# Revit family: Hager-Volta-IP30-Flush_mounted-vuoto-CH-it
name_source: partatom
category: Electrical Equipment
units: mm (PartAtom-declared; Revit-internal decimal feet)

## family parameters
Cut with Voids When Loaded = No
Host = Face
Panel Configuration = Two Columns, Circuits Across
Part Type = Panelboard
Room Calculation Point = No
Round Connector Dimension = Use Diameter
Shared = No

## types (5) — shared parameters
EF000003 - Tipo di montaggio = EV000383 - incassato
EF000007 - colore = EV000270 - grigio
EF000049 - profondità = 94 mm  [stored 0.308399 ft]
EF000116 - numero RAL = 7035
EF000118 - con piastra di montaggio = No
EF000218 - profondità di incasso = 90 mm  [stored 0.295276 ft]
EF000846 - larghezza di montaggio = 335 mm  [stored 1.09908 ft]
EF001062 - esecuzione EMC = Yes
EF001088 - possibilità di applicazione = Yes
EF001131 - profondità interna = 92 mm
EF001134 - barra DIN = No
EF001596 - Attacco Lampada = EV000139 - plastica
EF002950 - Numero moduli DIN = 12
EF006244 - coperchio/porta trasparente = No
EF006306 - con serratura = No
EF009212 - esecuzione coperchio = EV000116 - chiuso
EF015776 - Morsettiera di terra = No
EF015777 - Morsettiera neutra = No
EF015941 - Segnale di passaggio porta = No
HG000002 - Con porta = No
HG000003 - Gamma = Volta
HG000005 - Spessore = 3 mm  [stored 0.00984252 ft]
HG000006 - Ad incasso = Yes
HG000009 - Porta doppia a battente = No
HG000010 - Porte asimmetriche = No
HG000011 - File vuote nella parte basse = No
HG000017 - Distanza tra i poli = 18 mm  [stored 0.0590551 ft]
Manufacturer = Hager
Type Comments = Volta
zero-valued in all types: Default Elevation, HG000001 - Numero di colonne, HG000007 - Numero di colonne vuote, HG000008 - Numero di file vuote

## per-type parameters (varying)
| type | EF000008 - Larghezza | EF000040 - Altezza | EF000266 - numero di file | EF000332 - Altezza della parte incassata | HG000004 - Codice produttore | Model |
| incassato  L330 A355 P94.5 12 Unità di divisione - VU12NK | 330 mm | 355 mm | 1 | 346 mm | VU12NK | VU12NK |
| incassato  L330 A484 P94.5 12 Unità di divisione - VU24NK | 330 mm | 484 mm | 2 | 471 mm | VU24NK | VU24NK |
| incassato  L330 A609 P94.5 12 Unità di divisione - VU36NK | 330 mm | 609 mm | 3 | 596 mm | VU36NK | VU36NK |
| incassato  L330 A734 P94.5 12 Unità di divisione - VU48NK | 330 mm | 734 mm | 4 | 721 mm | VU48NK | VU48NK |
| incassato  L348 A880 P94.5 12 Unità di divisione - VU60NK | 348 mm  [stored 1.14173 ft] | 880 mm  [stored 2.88714 ft] | 5 | 846 mm  [stored 2.77559 ft] | VU60NK | VU60NK |

note: [stored X ft] marks values corroborated as IEEE doubles in the binary element streams (Revit-internal decimal feet)

## geometry (parser evidence)
native form markers: Sweep x17
no freeform markers — native parametric forms only
